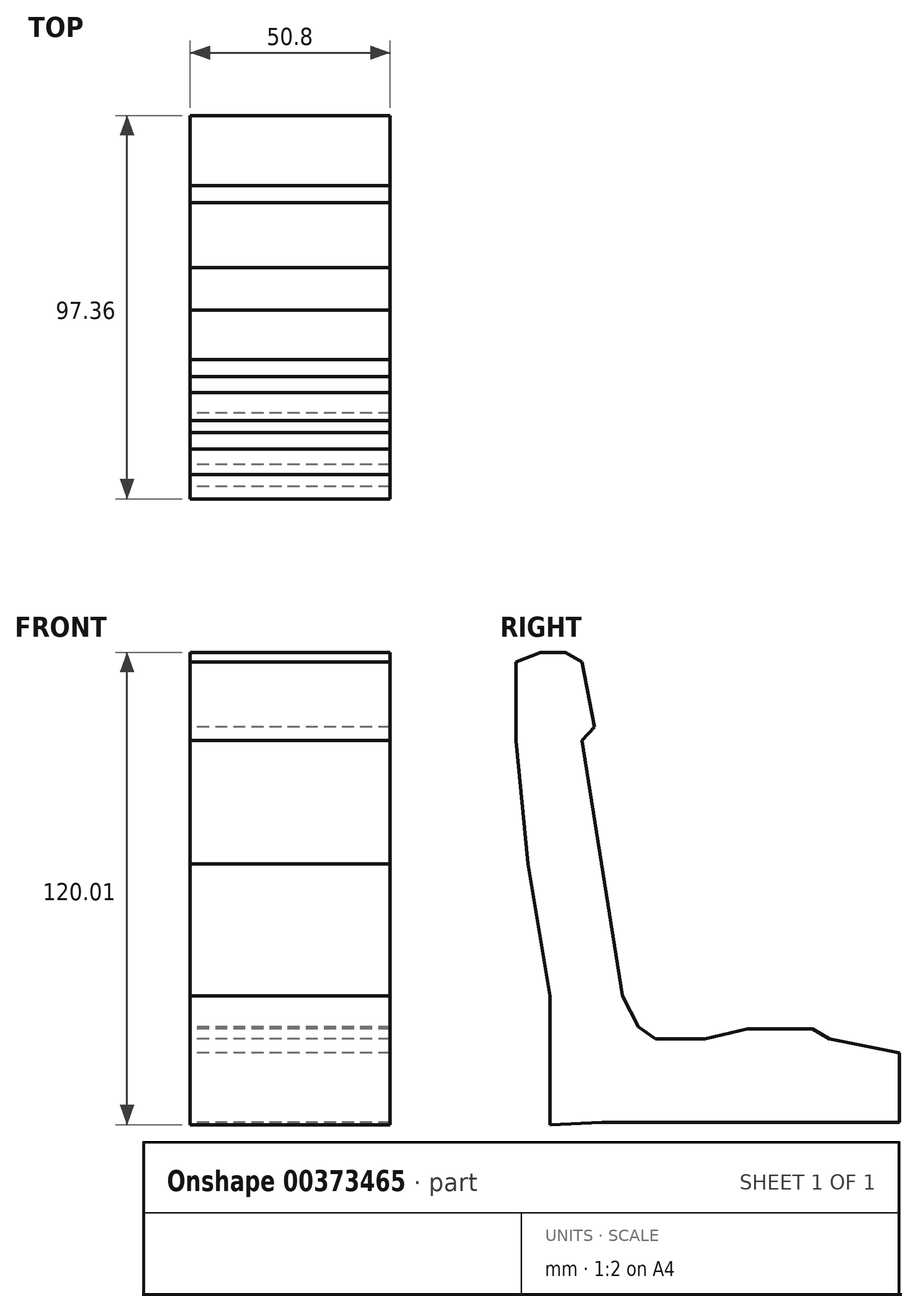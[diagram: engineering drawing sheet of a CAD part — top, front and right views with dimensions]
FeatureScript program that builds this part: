
annotation { "Feature Type Name" : "Feature", "Feature Type Description" : "" }
export const myFeature = defineFeature(function(context is Context, id is Id, definition is map)
    precondition{}
    {
        {
            var Q0;
            Q0=qCreatedBy(makeId("Right.planeOp"),FACE);
            var sketch = newSketch(context, id + "F0", { "sketchPlane" : qUnion([Q0])});
            skLineSegment(sketch, "E0", {"start": v(48.26, -29.37) * mm, "end": v(31.75, -29.37) * mm});
            skLineSegment(sketch, "E1", {"start": v(-5.18, -53.15) * mm, "end": v(70.36, -53.15) * mm});
            skLineSegment(sketch, "E2", {"start": v(70.36, -53.15) * mm, "end": v(70.36, -45.04) * mm});
            skLineSegment(sketch, "E3", {"start": v(70.36, -45.04) * mm, "end": v(70.36, -35.53) * mm});
            skLineSegment(sketch, "E4", {"start": v(70.36, -35.53) * mm, "end": v(52.63, -31.9) * mm});
            skLineSegment(sketch, "E5", {"start": v(52.63, -31.9) * mm, "end": v(48.26, -29.37) * mm});
            skLineSegment(sketch, "E6", {"start": v(48.26, -29.37) * mm, "end": v(40, -29.37) * mm});
            skLineSegment(sketch, "E7", {"start": v(10.5, -33.45) * mm, "end": v(4.06, -28.81) * mm});
            skLineSegment(sketch, "E8", {"start": v(4.06, -28.81) * mm, "end": v(0, -20.98) * mm});
            skLineSegment(sketch, "E9", {"start": v(0, -20.98) * mm, "end": v(-10.21, 43.92) * mm});
            skLineSegment(sketch, "E10", {"start": v(-10.21, 43.92) * mm, "end": v(-7.13, 47.28) * mm});
            skLineSegment(sketch, "E11", {"start": v(-7.13, 47.28) * mm, "end": v(-10.21, 63.78) * mm});
            skLineSegment(sketch, "E12", {"start": v(-10.21, 63.78) * mm, "end": v(-14.4, 66.3) * mm});
            skLineSegment(sketch, "E13", {"start": v(-14.4, 66.3) * mm, "end": v(-20.84, 66.3) * mm});
            skLineSegment(sketch, "E14", {"start": v(-20.84, 66.3) * mm, "end": v(-27, 63.78) * mm});
            skLineSegment(sketch, "E15", {"start": v(-27, 63.78) * mm, "end": v(-27, 43.92) * mm});
            skLineSegment(sketch, "E16", {"start": v(-27, 43.92) * mm, "end": v(-23.92, 12.59) * mm});
            skLineSegment(sketch, "E17", {"start": v(-23.92, 12.59) * mm, "end": v(-18.32, -20.98) * mm});
            skLineSegment(sketch, "E18", {"start": v(-18.32, -20.98) * mm, "end": v(-18.32, -53.71) * mm});
            skLineSegment(sketch, "E19", {"start": v(-5.18, -53.15) * mm, "end": v(-18.32, -53.71) * mm});
            skLineSegment(sketch, "E20", {"start": v(31.75, -29.37) * mm, "end": v(14.69, -33.45) * mm});
            skLineSegment(sketch, "E21", {"start": v(21, -31.94) * mm, "end": v(4.06, -31.94) * mm});
            skSolve(sketch);
        }
        {
            var Q0;
            {var subQ4=sQuery(id+"F0.wireOp",EDGE,"E0");Q0=makeQuery(id+"F0.imprint","IMPRINT",FACE,{"disambiguationData":[TD([[makeQuery(id+"F0.imprint","IMPRINT",EDGE,{"derivedFrom":subQ4}),1.0]])]});}
            extrude(context, id + "F1", {"entities" : qUnion([Q0]), "depth" : 127 * mm});
        }
        {
            var Q0;
            Q0=makeQuery(id+"F1.opExtrude","CAP_FACE",FACE,{"disambiguationData":[OSD([sQuery(id+"F0.wireOp",EDGE,"E0"),sQuery(id+"F0.wireOp",EDGE,"E1"),sQuery(id+"F0.wireOp",EDGE,"E2"),sQuery(id+"F0.wireOp",EDGE,"E3"),sQuery(id+"F0.wireOp",EDGE,"E4"),sQuery(id+"F0.wireOp",EDGE,"E5"),sQuery(id+"F0.wireOp",EDGE,"E6"),sQuery(id+"F0.wireOp",EDGE,"E7"),sQuery(id+"F0.wireOp",EDGE,"E8"),sQuery(id+"F0.wireOp",EDGE,"E9"),sQuery(id+"F0.wireOp",EDGE,"E10"),sQuery(id+"F0.wireOp",EDGE,"E11"),sQuery(id+"F0.wireOp",EDGE,"E12"),sQuery(id+"F0.wireOp",EDGE,"E13"),sQuery(id+"F0.wireOp",EDGE,"E14"),sQuery(id+"F0.wireOp",EDGE,"E15"),sQuery(id+"F0.wireOp",EDGE,"E16"),sQuery(id+"F0.wireOp",EDGE,"E17"),sQuery(id+"F0.wireOp",EDGE,"E18"),sQuery(id+"F0.wireOp",EDGE,"E19"),sQuery(id+"F0.wireOp",EDGE,"E20"),sQuery(id+"F0.wireOp",EDGE,"E21")])],"isStart":true});
            extrude(context, id + "F2", {"entities" : qUnion([Q0]), "operationType" : NewBodyOperationType.REMOVE, "oppositeDirection" : true, "depth" : 76.2 * mm});
        }
    });
